# Revit family: Sanitary_Toilets_Toto_MS642124CEFG-Nexus-1pc-Toilet
name_source: partatom
category: Plumbing Fixtures
units: mm (PartAtom-declared; Revit-internal decimal feet)

## family parameters
Cut with Voids When Loaded = No
Host = Face
OmniClass Number = 23.45.05.21.11
OmniClass Title = Water Closets
Part Type = Normal
Room Calculation Point = No
Round Connector Dimension = Use Diameter
Shared = No

## types (2) — shared parameters
Assembly Code = D2010
Cold Water Inlet Connection Diameter = 1"
Default Elevation = 0"
Depth = 28 9/16"
Description = Nexus 1pc Toilet
Edition number = 1
Flush Lever Finish = Toto - Chrome - Polished
Height = 27"
Keynote = 15410
Manufacturer = TOTO USA Inc.
Maximum Pressure (static) = 80.00 psi
Minimum Water Pressure (flowing) = 8.00 psi
Model = MS642234CEFG
Product Color = Available Colors: Cotton and Sedona Beige
Product Material = Toto - Vitreous China - Cotton
Sanitary Drain Connection Diameter = 2"
URL = http://www.totousa.com
Weight = 120.00 lb
Width = 17 1/2"
Z_Rough-In 12" = Rough-In : 12"
zero-valued in all types: CWFU, WFU

## per-type parameters (varying)
| type | Flush Rate | Z_Rough-In 14" |
| MS642124CEFG | 1.28 GPF | Rough-In : 12" |
| MS642124CUFG | 1.00 GPF | Rough-In : 14" |

## geometry (parser evidence)
native form markers: Sweep x7
no freeform markers — native parametric forms only
